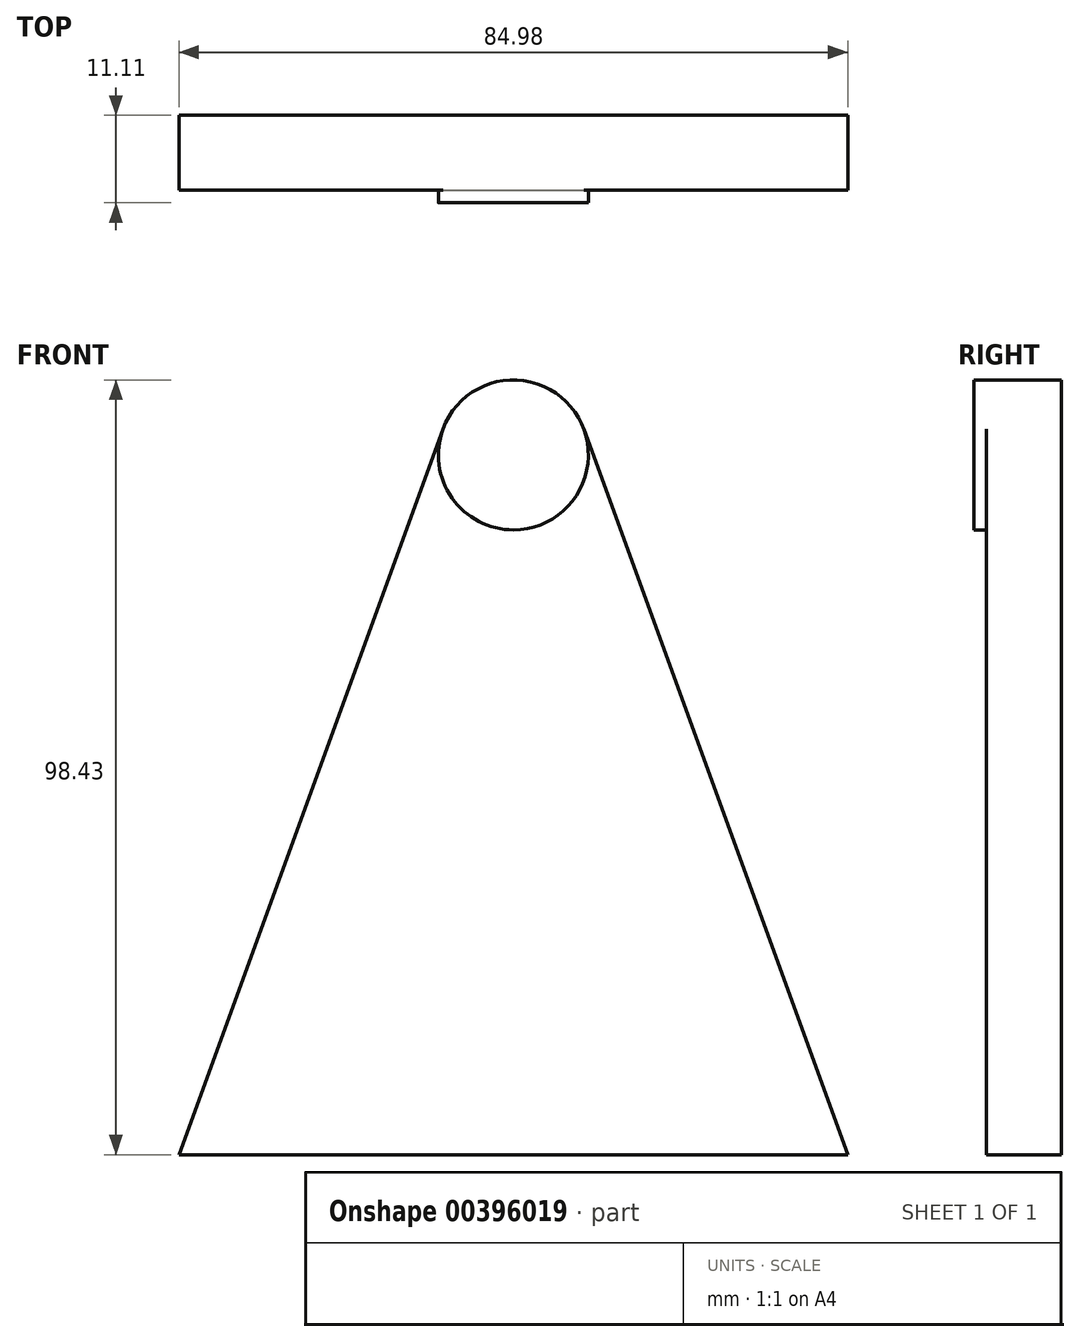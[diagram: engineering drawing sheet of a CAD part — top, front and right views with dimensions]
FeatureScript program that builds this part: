
annotation { "Feature Type Name" : "Feature", "Feature Type Description" : "" }
export const myFeature = defineFeature(function(context is Context, id is Id, definition is map)
    precondition{}
    {
        {
            var Q0;
            Q0=qCreatedBy(makeId("Front.planeOp"),FACE);
            var sketch = newSketch(context, id + "F0", { "sketchPlane" : qUnion([Q0])});
            skArc(sketch, "E0", {"start": v(8.95, 3.26) * mm, "mid": v(0, 9.53) * mm, "end": v(-8.95, 3.26) * mm});
            skLineSegment(sketch, "E1", {"start": v(-8.95, 3.26) * mm, "end": v(-42.5, -88.9) * mm});
            skLineSegment(sketch, "E2", {"start": v(-42.5, -88.9) * mm, "end": v(0, -88.9) * mm});
            skLineSegment(sketch, "E3.MirrorCS", {"start": v(8.95, 3.26) * mm, "end": v(42.5, -88.9) * mm});
            skLineSegment(sketch, "E4.MirrorCS", {"start": v(42.5, -88.9) * mm, "end": v(0, -88.9) * mm});
            skSolve(sketch);
        }
        {
            var Q0;
            Q0 = qSketchRegion(id + "F0", true);
            extrude(context, id + "F1", {"entities" : qUnion([Q0]), "depth" : 9.52 * mm, "offsetDistance" : 25.4 * mm});
        }
        {
            var Q0;
            Q0=makeQuery(id+"F1.opExtrude","CAP_FACE",FACE,{"disambiguationData":[OSD([sQuery(id+"F0.wireOp",EDGE,"E0"),sQuery(id+"F0.wireOp",EDGE,"E1"),sQuery(id+"F0.wireOp",EDGE,"E2"),sQuery(id+"F0.wireOp",EDGE,"E3.MirrorCS"),sQuery(id+"F0.wireOp",EDGE,"E4.MirrorCS")])],"isStart":false});
            var sketch = newSketch(context, id + "F2", { "sketchPlane" : qUnion([Q0])});
            skCircle(sketch, "E5", {"center": v(0, 0) * mm, "radius": 9.53 * mm});
            skSolve(sketch);
        }
        {
            var Q0;
            Q0 = qSketchRegion(id + "F2", true);
            extrude(context, id + "F3", {"entities" : qUnion([Q0]), "operationType" : NewBodyOperationType.ADD, "depth" : 1.59 * mm, "offsetDistance" : 25.4 * mm});
        }
    });
